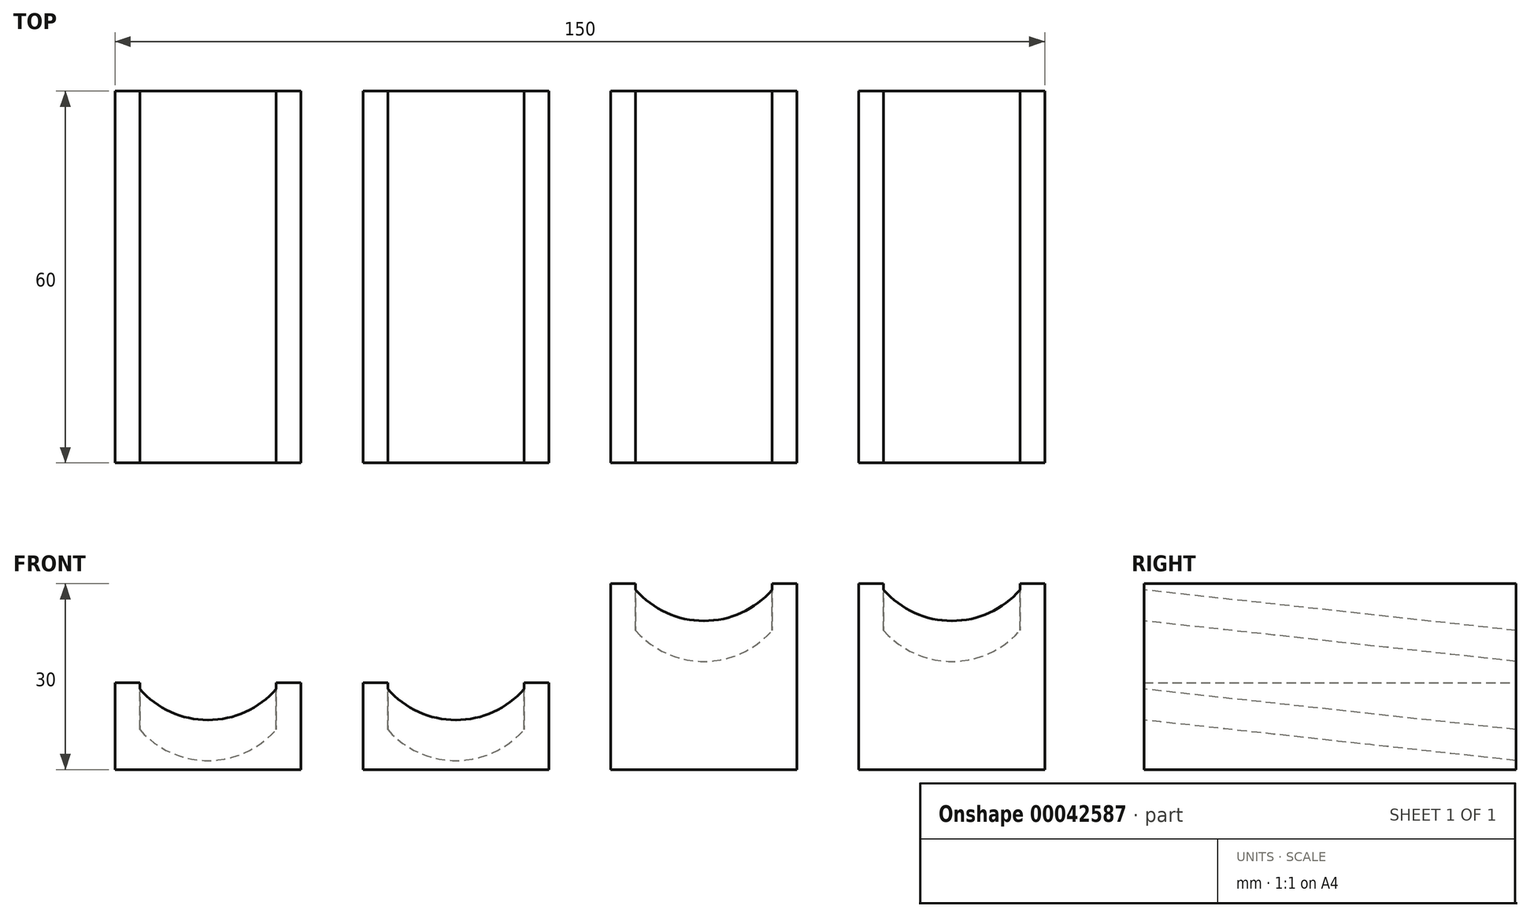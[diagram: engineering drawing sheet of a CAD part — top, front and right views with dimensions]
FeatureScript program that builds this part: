
annotation { "Feature Type Name" : "Feature", "Feature Type Description" : "" }
export const myFeature = defineFeature(function(context is Context, id is Id, definition is map)
    precondition{}
    {
        {
            var Q0;
            Q0=qCreatedBy(makeId("Top.planeOp"),FACE);
            var sketch = newSketch(context, id + "F0", { "sketchPlane" : qUnion([Q0])});
            skLineSegment(sketch, "E0.rect.bottom", {"start": v(15, -30) * mm, "end": v(-15, -30) * mm});
            skLineSegment(sketch, "E0.rect.top", {"start": v(15, 30) * mm, "end": v(-15, 30) * mm});
            skLineSegment(sketch, "E0.rect.left", {"start": v(15, -30) * mm, "end": v(15, 30) * mm});
            skLineSegment(sketch, "E0.rect.right", {"start": v(-15, -30) * mm, "end": v(-15, 30) * mm});
            skPoint(sketch, "E0.rect.middle", {"position": v(0, 0) * mm});
            skSolve(sketch);
        }
        {
            var Q0;
            Q0 = qSketchRegion(id + "F0", true);
            extrude(context, id + "F1", {"entities" : qUnion([Q0]), "depth" : 30 * mm});
        }
        {
            var Q0;
            Q0=makeQuery(id+"F1.opExtrude","SWEPT_FACE",FACE,{"disambiguationData":[OSD([sQuery(id+"F0.wireOp",EDGE,"E0.rect.bottom")])]});
            var sketch = newSketch(context, id + "F2", { "sketchPlane" : qUnion([Q0])});
            skLineSegment(sketch, "E1", {"start": v(-11, 30) * mm, "end": v(11, 30) * mm});
            skPoint(sketch, "E2", {"position": v(0, 30) * mm});
            skLineSegment(sketch, "E3", {"start": v(-11, 30) * mm, "end": v(-11, 29) * mm});
            skLineSegment(sketch, "E4", {"start": v(11, 30) * mm, "end": v(11, 29) * mm});
            skArc(sketch, "E5", {"start": v(-11, 29) * mm, "mid": v(0, 24) * mm, "end": v(11, 29) * mm});
            skLineSegment(sketch, "E6", {"start": v(0, 30) * mm, "end": v(0, 24) * mm, "construction": true});
            skSolve(sketch);
        }
        {
            var Q0;
            Q0=qCreatedBy(makeId("Front.planeOp"),FACE);
            cPlane(context, id + "F3", {"entities" : qUnion([Q0]), "cplaneType" : CPlaneType.OFFSET, "offset" : 190 * mm, "oppositeDirection" : true, "width" : 150 * mm, "height" : 150 * mm});
        }
        {
            var Q0;
            Q0=qCreatedBy(id+"F3.planeOp",FACE);
            var sketch = newSketch(context, id + "F4", { "sketchPlane" : qUnion([Q0])});
            skLineSegment(sketch, "E7.0", {"start": v(-11, 30) * mm, "end": v(11, 30) * mm});
            skLineSegment(sketch, "E8", {"start": v(11, 30) * mm, "end": v(11, 5) * mm});
            skLineSegment(sketch, "E9", {"start": v(-11, 30) * mm, "end": v(-11, 5) * mm});
            skPoint(sketch, "E10.0", {"position": v(0, 0) * mm});
            skArc(sketch, "E11", {"start": v(-11, 5) * mm, "mid": v(0, 0) * mm, "end": v(11, 5) * mm});
            skSolve(sketch);
        }
        {
            var Q1;
            Q1=makeQuery(id+"F4.imprint","IMPRINT",FACE,{"disambiguationData":[TD([[makeQuery(id+"F4.imprint","IMPRINT",EDGE,{"derivedFrom":sQuery(id+"F4.wireOp",EDGE,"E7.0")}),-1.0]])]});
            var Q2;
            Q2=makeQuery(id+"F2.imprint","IMPRINT",FACE,{"disambiguationData":[TD([[makeQuery(id+"F2.imprint","IMPRINT",EDGE,{"derivedFrom":sQuery(id+"F2.wireOp",EDGE,"E1")}),1.0]])]});
            loft(context, id + "F5", {"operationType" : NewBodyOperationType.REMOVE, "sheetProfilesArray" : [{ "sheetProfileEntities" : qUnion([Q1]) }, { "sheetProfileEntities" : qUnion([Q2]) }]});
        }
        {
            var Q0;
            Q0=makeQuery(id+"F1.opExtrude","SWEPT_BODY",BODY,{"disambiguationData":[OSD([sQuery(id+"F0.wireOp",EDGE,"E0.rect.bottom"),sQuery(id+"F0.wireOp",EDGE,"E0.rect.top"),sQuery(id+"F0.wireOp",EDGE,"E0.rect.left"),sQuery(id+"F0.wireOp",EDGE,"E0.rect.right")])]});
            transform(context, id + "F6", {"entities" : qUnion([Q0]), "transformType" : TransformType.TRANSLATION_3D, "dx" : 40 * mm, "dy" : 0 * mm, "dz" : 0 * mm, "makeCopy" : true});
        }
        {
            var Q0;
            Q0=makeQuery(id+"F1.opExtrude","SWEPT_BODY",BODY,{"disambiguationData":[OSD([sQuery(id+"F0.wireOp",EDGE,"E0.rect.bottom"),sQuery(id+"F0.wireOp",EDGE,"E0.rect.top"),sQuery(id+"F0.wireOp",EDGE,"E0.rect.left"),sQuery(id+"F0.wireOp",EDGE,"E0.rect.right")])]});
            var Q1;
            Q1=makeQuery(id+"F6.opPattern","COPY",BODY,{"derivedFrom":makeQuery(id+"F1.opExtrude","SWEPT_BODY",BODY,{"disambiguationData":[OSD([sQuery(id+"F0.wireOp",EDGE,"E0.rect.bottom"),sQuery(id+"F0.wireOp",EDGE,"E0.rect.top"),sQuery(id+"F0.wireOp",EDGE,"E0.rect.left"),sQuery(id+"F0.wireOp",EDGE,"E0.rect.right")])]}),"instanceName":"1"});
            transform(context, id + "F7", {"entities" : qUnion([Q0, Q1]), "transformType" : TransformType.TRANSLATION_3D, "dx" : -80 * mm, "dy" : 0 * mm, "dz" : 0 * mm, "makeCopy" : true});
        }
        {
            var Q0;
            Q0=makeQuery(id+"F7.opPattern","COPY",FACE,{"derivedFrom":makeQuery(id+"F6.opPattern","COPY",FACE,{"derivedFrom":makeQuery(id+"F1.opExtrude","SWEPT_FACE",FACE,{"disambiguationData":[OSD([sQuery(id+"F0.wireOp",EDGE,"E0.rect.top")])]}),"instanceName":"1"}),"instanceName":"1"});
            var sketch = newSketch(context, id + "F8", { "sketchPlane" : qUnion([Q0])});
            skLineSegment(sketch, "E12.bottom", {"start": v(25, 0) * mm, "end": v(110.36, 0) * mm});
            skLineSegment(sketch, "E12.top", {"start": v(25, 16) * mm, "end": v(110.36, 16) * mm});
            skLineSegment(sketch, "E12.left", {"start": v(25, 0) * mm, "end": v(25, 16) * mm});
            skLineSegment(sketch, "E12.right", {"start": v(110.36, 0) * mm, "end": v(110.36, 16) * mm});
            skSolve(sketch);
        }
        {
            var Q0;
            Q0 = qSketchRegion(id + "F8", true);
            extrude(context, id + "F9", {"entities" : qUnion([Q0]), "operationType" : NewBodyOperationType.REMOVE, "endBound" : BoundingType.THROUGH_ALL, "oppositeDirection" : true, "depth" : 25 * mm});
        }
        {
            var Q0;
            Q0=makeQuery(id+"F7.opPattern","COPY",BODY,{"derivedFrom":makeQuery(id+"F6.opPattern","COPY",BODY,{"derivedFrom":makeQuery(id+"F1.opExtrude","SWEPT_BODY",BODY,{"disambiguationData":[OSD([sQuery(id+"F0.wireOp",EDGE,"E0.rect.bottom"),sQuery(id+"F0.wireOp",EDGE,"E0.rect.top"),sQuery(id+"F0.wireOp",EDGE,"E0.rect.left"),sQuery(id+"F0.wireOp",EDGE,"E0.rect.right")])]}),"instanceName":"1"}),"instanceName":"1"});
            var Q1;
            Q1=makeQuery(id+"F7.opPattern","COPY",BODY,{"derivedFrom":makeQuery(id+"F1.opExtrude","SWEPT_BODY",BODY,{"disambiguationData":[OSD([sQuery(id+"F0.wireOp",EDGE,"E0.rect.bottom"),sQuery(id+"F0.wireOp",EDGE,"E0.rect.top"),sQuery(id+"F0.wireOp",EDGE,"E0.rect.left"),sQuery(id+"F0.wireOp",EDGE,"E0.rect.right")])]}),"instanceName":"1"});
            transform(context, id + "F10", {"entities" : qUnion([Q0, Q1]), "transformType" : TransformType.TRANSLATION_3D, "dx" : 0 * mm, "dy" : 0 * mm, "dz" : -16 * mm, "makeCopy" : false});
        }
    });
